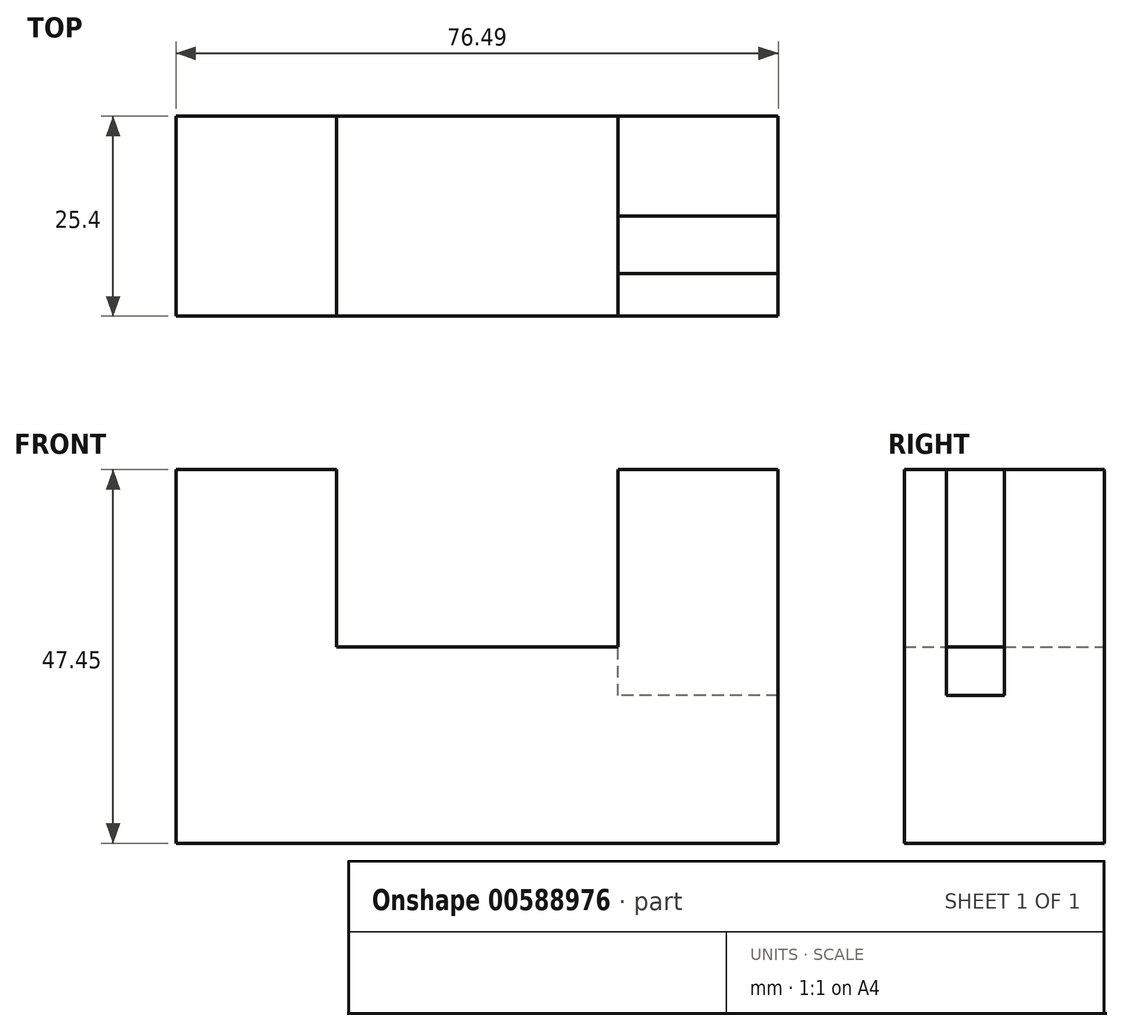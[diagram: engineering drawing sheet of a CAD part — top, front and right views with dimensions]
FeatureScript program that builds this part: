
annotation { "Feature Type Name" : "Feature", "Feature Type Description" : "" }
export const myFeature = defineFeature(function(context is Context, id is Id, definition is map)
    precondition{}
    {
        {
            var Q0;
            Q0=qCreatedBy(makeId("Front.planeOp"),FACE);
            var sketch = newSketch(context, id + "F0", { "sketchPlane" : qUnion([Q0])});
            skLineSegment(sketch, "E0.bottom", {"start": v(0, 47.45) * mm, "end": v(20.37, 47.45) * mm});
            skLineSegment(sketch, "E0.top", {"start": v(0, 0) * mm, "end": v(76.49, 0) * mm});
            skLineSegment(sketch, "E0.left", {"start": v(0, 47.45) * mm, "end": v(0, 0) * mm});
            skLineSegment(sketch, "E0.right", {"start": v(76.49, 47.45) * mm, "end": v(76.49, 0) * mm});
            skLineSegment(sketch, "E1.bottom", {"start": v(56.12, 24.92) * mm, "end": v(20.37, 24.92) * mm});
            skLineSegment(sketch, "E1.left", {"start": v(56.12, 24.92) * mm, "end": v(56.12, 47.45) * mm});
            skLineSegment(sketch, "E1.right", {"start": v(20.37, 24.92) * mm, "end": v(20.37, 47.45) * mm});
            skPoint(sketch, "E1.middle", {"position": v(38.24, 36.18) * mm});
            skPoint(sketch, "E1.middle.positionSnap0", {"position": v(38.24, 47.45) * mm});
            skPoint(sketch, "E1.centerSnap0", {"position": v(38.24, 47.45) * mm});
            skLineSegment(sketch, "E2.trimOffspring", {"start": v(56.12, 47.45) * mm, "end": v(76.49, 47.45) * mm});
            skSolve(sketch);
        }
        {
            var Q0;
            Q0=makeQuery(id+"F0.imprint","IMPRINT",FACE,{"disambiguationData":[TD([[makeQuery(id+"F0.imprint","IMPRINT",EDGE,{"derivedFrom":sQuery(id+"F0.wireOp",EDGE,"E0.bottom")}),-1.0]])]});
            extrude(context, id + "F1", {"entities" : qUnion([Q0]), "depth" : 25.4 * mm, "offsetDistance" : 25.4 * mm});
        }
        {
            var Q0;
            Q0=makeQuery(id+"F1.opExtrude","SWEPT_FACE",FACE,{"disambiguationData":[OSD([sQuery(id+"F0.wireOp",EDGE,"E2.trimOffspring")])]});
            var sketch = newSketch(context, id + "F2", { "sketchPlane" : qUnion([Q0])});
            skLineSegment(sketch, "E3.bottom", {"start": v(76.49, -9.68) * mm, "end": v(56.12, -9.68) * mm});
            skLineSegment(sketch, "E3.top", {"start": v(76.49, -19.34) * mm, "end": v(56.12, -19.34) * mm});
            skLineSegment(sketch, "E3.left", {"start": v(76.49, -9.68) * mm, "end": v(76.49, -19.34) * mm});
            skLineSegment(sketch, "E3.right", {"start": v(56.12, -9.68) * mm, "end": v(56.12, -19.34) * mm});
            skPoint(sketch, "E3.middle", {"position": v(66.3, -14.51) * mm});
            skPoint(sketch, "E3.middle.positionSnap0", {"position": v(66.3, -25.4) * mm});
            skPoint(sketch, "E3.centerSnap0", {"position": v(66.3, -25.4) * mm});
            skSolve(sketch);
        }
        {
            var Q0;
            Q0 = qSketchRegion(id + "F2", true);
            extrude(context, id + "F3", {"entities" : qUnion([Q0]), "operationType" : NewBodyOperationType.REMOVE, "depth" : 25.4 * mm, "offsetDistance" : 25.4 * mm});
        }
        {
            var Q0;
            Q0=makeQuery(id+"F1.opExtrude","SWEPT_FACE",FACE,{"disambiguationData":[OSD([sQuery(id+"F0.wireOp",EDGE,"E2.trimOffspring")])]});
            var sketch = newSketch(context, id + "F4", { "sketchPlane" : qUnion([Q0])});
            skLineSegment(sketch, "E4.bottom", {"start": v(61.97, -25.4) * mm, "end": v(70.63, -25.4) * mm});
            skLineSegment(sketch, "E4.top", {"start": v(61.97, -4.14) * mm, "end": v(70.63, -4.14) * mm});
            skLineSegment(sketch, "E4.left", {"start": v(61.97, -25.4) * mm, "end": v(61.97, -4.14) * mm});
            skLineSegment(sketch, "E4.right", {"start": v(70.63, -25.4) * mm, "end": v(70.63, -4.14) * mm});
            skPoint(sketch, "E4.middle", {"position": v(66.3, -14.77) * mm});
            skPoint(sketch, "E4.middle.positionSnap0", {"position": v(66.3, -25.4) * mm});
            skPoint(sketch, "E4.centerSnap0", {"position": v(66.3, -25.4) * mm});
            skSolve(sketch);
        }
        {
            var Q0;
            Q0 = qSketchRegion(id + "F4", true);
            extrude(context, id + "F5", {"entities" : qUnion([Q0]), "operationType" : NewBodyOperationType.ADD, "oppositeDirection" : true, "depth" : 25.15 * mm, "offsetDistance" : 25.4 * mm});
        }
        {
            var Q0;
            Q0=makeQuery(id+"F1.opExtrude","SWEPT_FACE",FACE,{"disambiguationData":[OSD([sQuery(id+"F0.wireOp",EDGE,"E2.trimOffspring")])]});
            var sketch = newSketch(context, id + "F6", { "sketchPlane" : qUnion([Q0])});
            skLineSegment(sketch, "E5.bottom", {"start": v(76.49, -12.7) * mm, "end": v(56.12, -12.7) * mm});
            skLineSegment(sketch, "E5.top", {"start": v(76.49, -20) * mm, "end": v(56.12, -20) * mm});
            skLineSegment(sketch, "E5.left", {"start": v(76.49, -12.7) * mm, "end": v(76.49, -20) * mm});
            skLineSegment(sketch, "E5.right", {"start": v(56.12, -12.7) * mm, "end": v(56.12, -20) * mm});
            skSolve(sketch);
        }
        {
            var Q0;
            Q0 = qSketchRegion(id + "F6", true);
            extrude(context, id + "F7", {"entities" : qUnion([Q0]), "operationType" : NewBodyOperationType.REMOVE, "oppositeDirection" : true, "depth" : 28.7 * mm, "offsetDistance" : 25.4 * mm});
        }
    });
